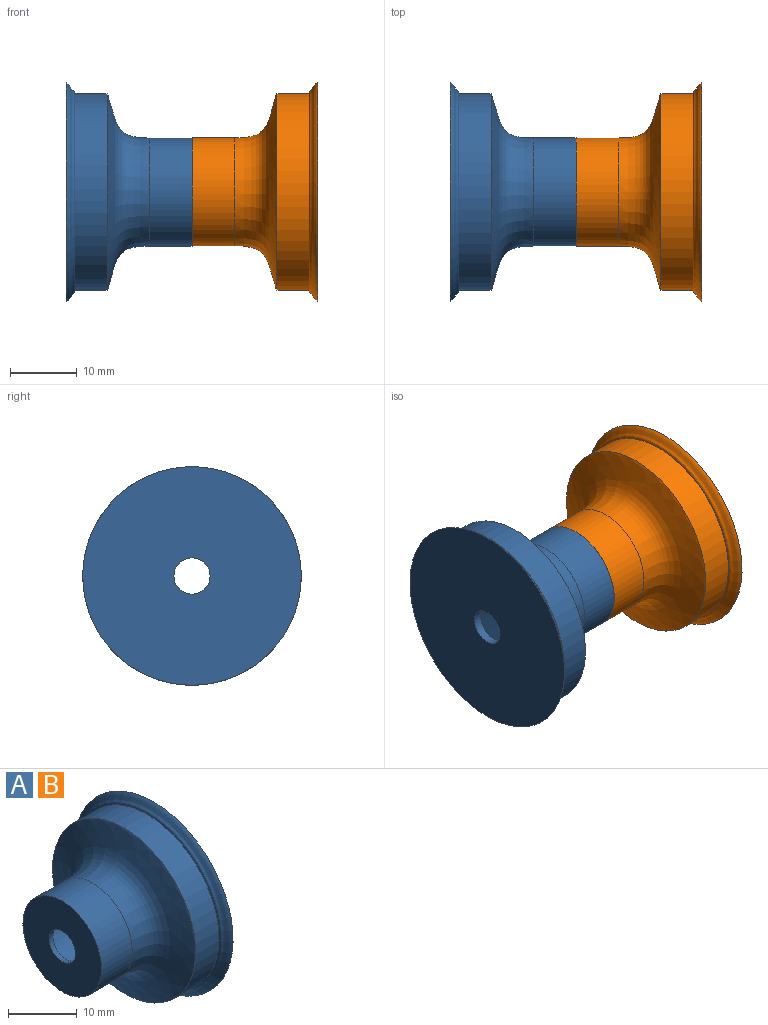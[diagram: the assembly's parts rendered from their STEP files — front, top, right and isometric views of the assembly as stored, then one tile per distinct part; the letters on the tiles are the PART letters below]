
ASSEMBLY  parts=2 mates=1
PART A: 13 faces, bbox 18.8x32.7x32.7 mm
  f0: cylinder r=14.7mm len=29.4mm, axis (-1,0,0), area 443.3mm2, adj f1,f12
  f1: revolved ~29.4x29.4mm, area 682.1mm2, adj f0,f2
  f2: cylinder r=8.07mm len=16.14mm, axis (-1,0,0), area 319.5mm2, adj f1,f3
  f3: plane 16.14x16.14mm, normal (-1,0,0), area 181.8mm2, adj f2,f4
  f4: cylinder r=2.7mm len=5.4mm, axis (-1,0,0), area 13.5mm2, adj f3,f5
  f5: plane 14.96x14.96mm, normal (1,0,0), area 153mm2, adj f4,f6
  f6: cylinder r=7.48mm len=14.96mm, axis (-1,0,0), area 495.8mm2, adj f5,f7
  f7: cone r=7.48mm half-angle=67.3deg, axis (1,0,0), area 337.5mm2, adj f6,f8
  f8: cylinder r=12.45mm len=24.91mm, axis (-1,0,0), area 320.6mm2, adj f7,f9
  f9: plane 24.91x24.91mm, normal (-1,0,0), area 464.3mm2, adj f8,f10
  f10: cylinder r=2.7mm len=5.4mm, axis (-1,0,0), area 20.9mm2, adj f9,f11
  f11: plane 32.66x32.66mm, normal (1,0,0), area 814.8mm2, adj f10,f12
  f12: revolved ~32.66x32.66mm, area 206.3mm2, adj f0,f11
PART B: same geometry as A
PLACE A rot(axis=(0,1,0),180deg) t=(23.85,-7.36,6.91)mm
PLACE B t=(23.85,-7.36,6.91)mm
MATE revolute A.f0 <-> B.f0  axis (1,0,0) through (23.85,-7.36,6.91)mm
